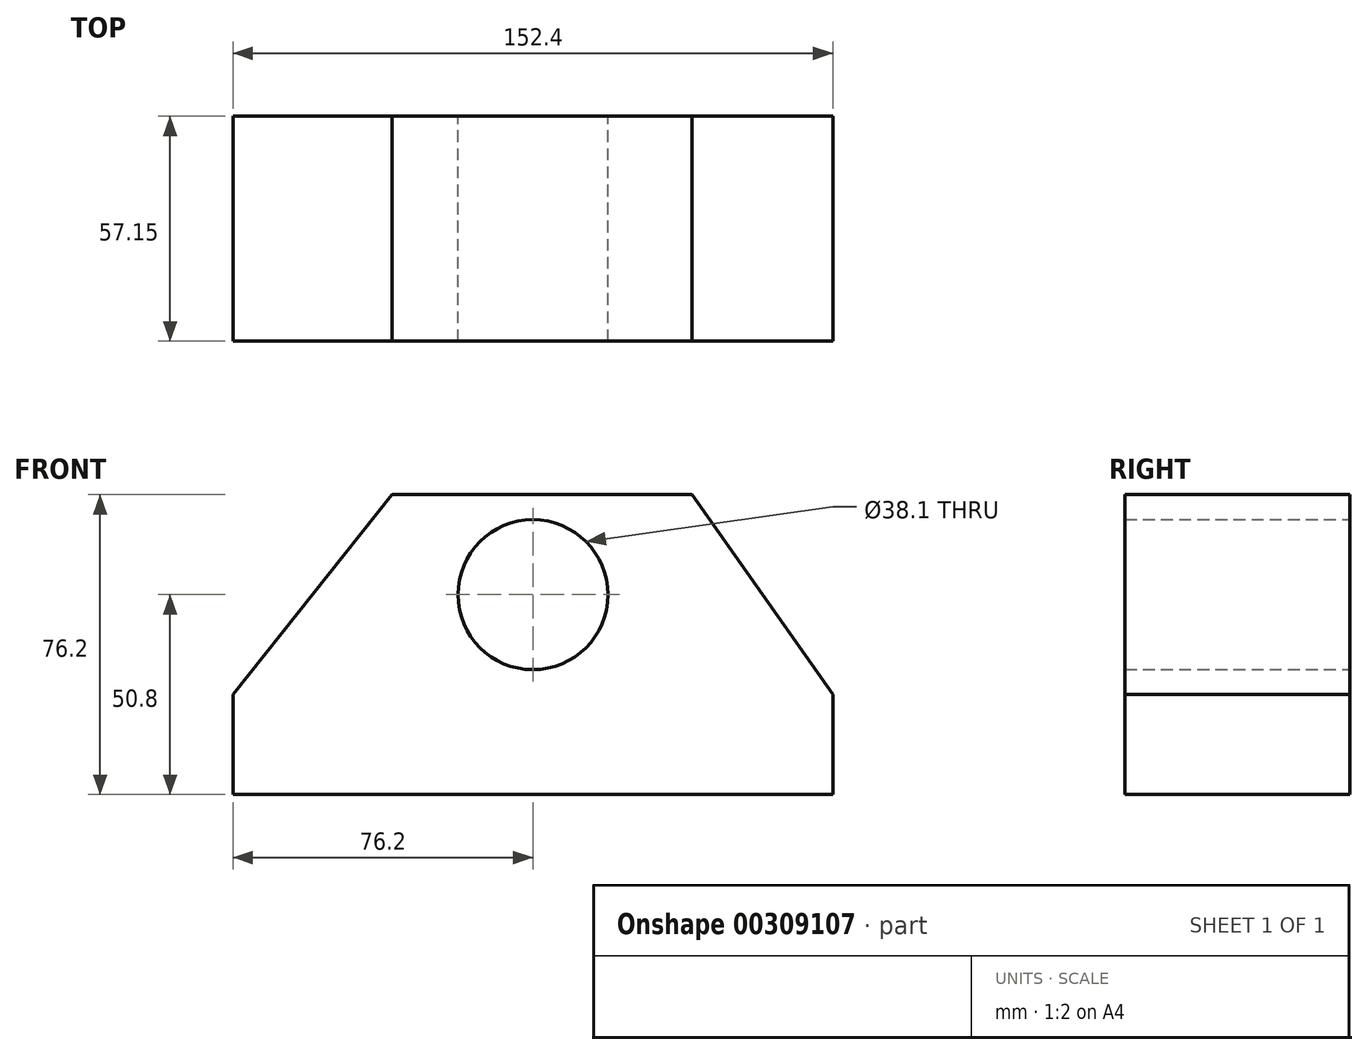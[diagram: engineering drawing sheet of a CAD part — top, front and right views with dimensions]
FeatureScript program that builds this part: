
annotation { "Feature Type Name" : "Feature", "Feature Type Description" : "" }
export const myFeature = defineFeature(function(context is Context, id is Id, definition is map)
    precondition{}
    {
        {
            var Q0;
            Q0=qCreatedBy(makeId("Front.planeOp"),FACE);
            var sketch = newSketch(context, id + "F0", { "sketchPlane" : qUnion([Q0])});
            skLineSegment(sketch, "E0", {"start": v(76.2, 0) * mm, "end": v(-76.2, 0) * mm});
            skLineSegment(sketch, "E1", {"start": v(-76.2, 0) * mm, "end": v(-76.2, 25.4) * mm});
            skLineSegment(sketch, "E2", {"start": v(76.2, 0) * mm, "end": v(76.2, 25.4) * mm});
            skLineSegment(sketch, "E3", {"start": v(76.2, 25.4) * mm, "end": v(40.39, 76.2) * mm});
            skLineSegment(sketch, "E4", {"start": v(-76.2, 25.4) * mm, "end": v(-35.81, 76.2) * mm});
            skLineSegment(sketch, "E5", {"start": v(-35.81, 76.2) * mm, "end": v(40.39, 76.2) * mm});
            skCircle(sketch, "E6", {"center": v(0, 50.8) * mm, "radius": 19.05 * mm});
            skSolve(sketch);
        }
        {
            var Q0;
            Q0 = qSketchRegion(id + "F0", true);
            extrude(context, id + "F1", {"entities" : qUnion([Q0]), "depth" : 57.15 * mm});
        }
    });
